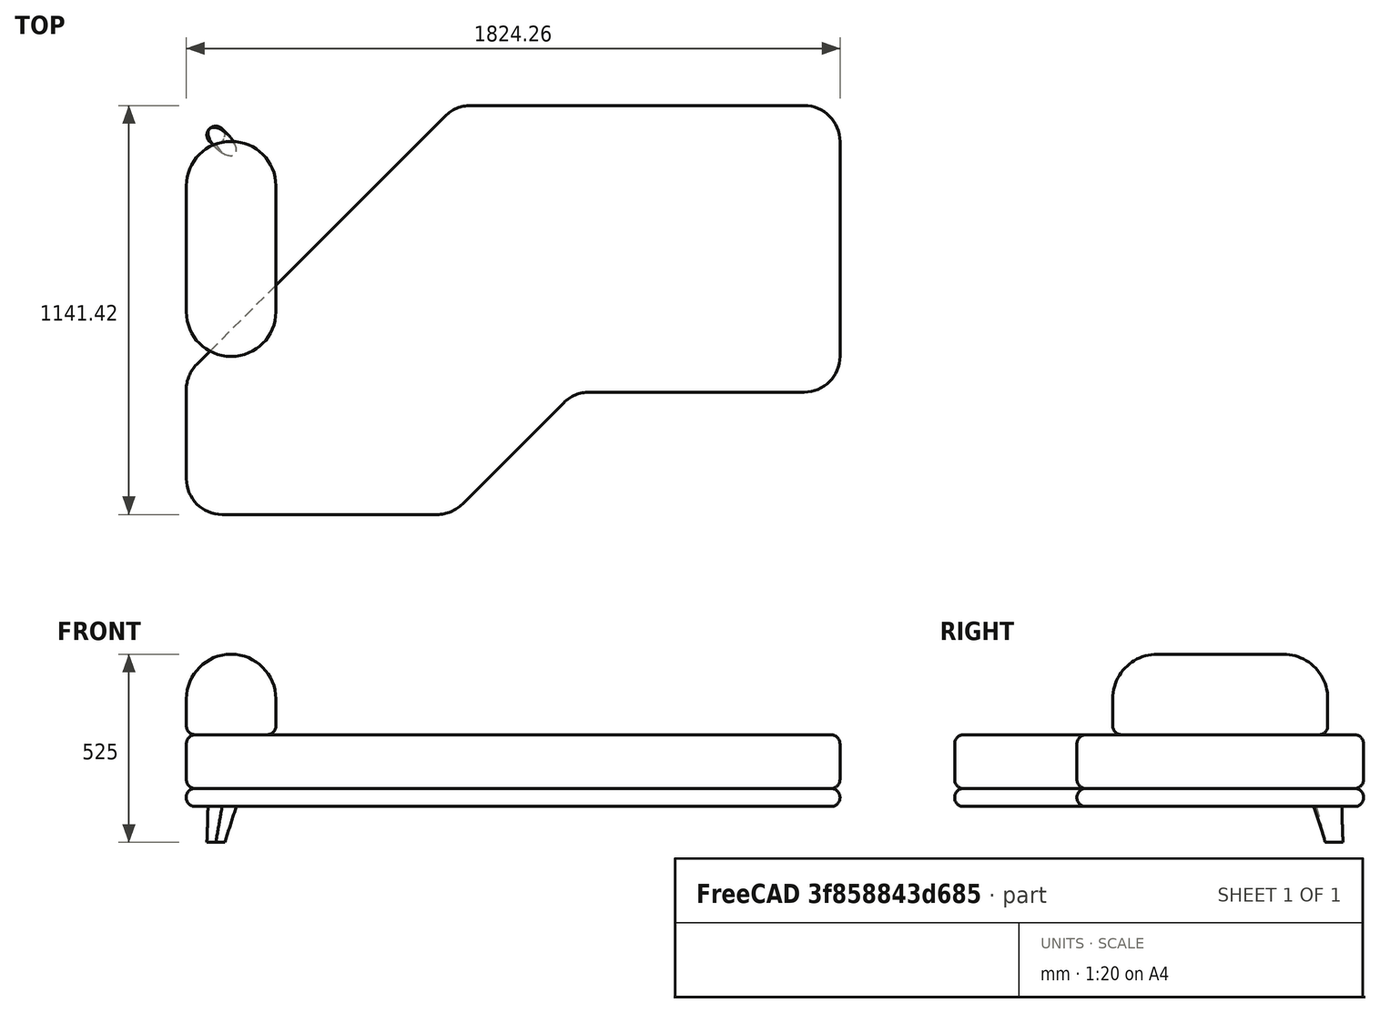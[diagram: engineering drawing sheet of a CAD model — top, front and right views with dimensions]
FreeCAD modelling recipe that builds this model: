
FCSTD DOCUMENT  (FreeCAD 1.0R39319 (Git))
Label: Drawing room Sofa corner
License: All rights reserved
objects: App::Link×10, App::FeaturePython×10, Sketcher::SketchObject×5, PartDesign::Fillet×4, PartDesign::Body×4, PartDesign::Pad×3, PartDesign::Plane×1, PartDesign::AdditiveLoft×1, Assembly::JointGroup×1, Assembly::AssemblyObject×1
note: 39 computed .brp shape members not serialized (recipe doc carries the construction recipe); baked Part::Feature solids carry a one-line shape summary decoded from their .brp

FEATURE [Sketcher::SketchObject] Sketch
  ArcFitTolerance = 1e-06
  AttachmentSupport = -> [XY_Plane]
  FullyConstrained = true
  MakeInternals = false
  MapMode = 5
  sketch-geometry (15):
    g0: ArcOfCircle CenterX=1724.26 CenterY=-100 CenterZ=0 NormalX=0 NormalY=0 NormalZ=1 AngleXU=0 Radius=100 StartAngle=1e-16 EndAngle=1.5708
    g1: LineSegment StartX=1824.26 StartY=-100 StartZ=0 EndX=1824.26 EndY=-700 EndZ=0
    g2: ArcOfCircle CenterX=1724.26 CenterY=-700 CenterZ=0 NormalX=0 NormalY=0 NormalZ=1 AngleXU=0 Radius=100 StartAngle=4.71239 EndAngle=6.28319
    g3: LineSegment StartX=1724.26 StartY=-800 StartZ=0 EndX=1124.26 EndY=-800 EndZ=0
    g4: ArcOfCircle CenterX=1124.26 CenterY=-900 CenterZ=0 NormalX=0 NormalY=0 NormalZ=1 AngleXU=0 Radius=100 StartAngle=1.5708 EndAngle=2.35619
    g5: LineSegment StartX=1053.55 StartY=-829.289 StartZ=0 EndX=770.711 EndY=-1112.13 EndZ=0
    g6: ArcOfCircle CenterX=700 CenterY=-1041.42 CenterZ=0 NormalX=0 NormalY=0 NormalZ=1 AngleXU=0 Radius=100 StartAngle=4.71239 EndAngle=5.49779
    g7: ArcOfCircle CenterX=100 CenterY=-792.893 CenterZ=0 NormalX=0 NormalY=0 NormalZ=1 AngleXU=0 Radius=100 StartAngle=2.35619 EndAngle=3.14159
    g8: LineSegment StartX=29.2893 StartY=-722.183 StartZ=0 EndX=722.183 EndY=-29.2893 EndZ=0
    g9: ArcOfCircle CenterX=792.893 CenterY=-100 CenterZ=0 NormalX=0 NormalY=0 NormalZ=1 AngleXU=0 Radius=100 StartAngle=1.5708 EndAngle=2.35619
    g10: LineSegment StartX=1724.26 StartY=0 StartZ=0 EndX=792.893 EndY=0 EndZ=0
    g11: LineSegment StartX=700 StartY=-1141.42 StartZ=0 EndX=100 EndY=-1141.42 EndZ=0
    g12: ArcOfCircle CenterX=100 CenterY=-1041.42 CenterZ=0 NormalX=0 NormalY=0 NormalZ=1 AngleXU=0 Radius=100 StartAngle=3.14159 EndAngle=4.71239
    g13: LineSegment StartX=0 StartY=-1041.42 StartZ=0 EndX=0 EndY=-792.893 EndZ=0
    g14: LineSegment [constr] StartX=0 StartY=-751.472 StartZ=0 EndX=751.472 EndY=-1.369e-13 EndZ=0
  constraints (42):
    c: Tangent(g0,g1) = 1.5708
    c: Tangent(g1,g2) = 1.5708
    c: Tangent(g2,g3) = 1.5708
    c: Tangent(g3,g4) = -1.5708
    c: Tangent(g4,g5) = -1.5708
    c: Tangent(g5,g6) = 1.5708
    c: Tangent(g7,g8) = 1.5708
    c: Tangent(g8,g9) = 1.5708
    c: Tangent(g10,g0) = -1.5708
    c: Tangent(g9,g10) = -1.5708
    c: Horizontal(g10)
    c: Vertical(g1)
    c: Horizontal(g3)
    c: Angle(g4) = 0.785398
    c: Radius(g2) = 100
    c: Radius(g0) = 100
    c: Radius(g9) = 100
    c: Parallel(g8,g5)
    c: Radius(g6) = 100
    c: Radius(g7) = 100
    c: Radius(g4) = 100
    c: Tangent(g6,g11) = 1.5708
    c: Tangent(g11,g12) = 1.5708
    c: Tangent(g12,g13) = 1.5708
    c: Vertical(g13)
    c: Horizontal(g11)
    c: Tangent(g7,g13) = 1.5708
    c: Radius(g12) = 100
    c: Distance(g1) = 600
    c: Distance(g11) = 600
    c: Distance(g3) = 600
    c: Distance(g5) = 400
    c: PointOnObject(g9,g-1)
    c: PointOnObject(g7,g-2)
    c: Distance(g4,g8) = 800
    c: PointOnObject(g14,g-2)
    c: PointOnObject(g14,g-1)
    c: PointOnObject(g14,g8)
    c: PointOnObject(g14,g8)
    c: Distance(g14,g-1) = 751.472
    c: Distance(g0,g-2) = 1824.26
    c: Distance(g11,g-1) = 1141.42
FEATURE [PartDesign::Pad] Pad
  Direction = (0,0,1)
  Length = 50
  Length2 = 10
  Profile = -> Sketch
  ReferenceAxis = -> Sketch [N_Axis]
  Refine = true
  Suppressed = false
  Type = 0
FEATURE [Sketcher::SketchObject] Sketch001
  ArcFitTolerance = 1e-06
  AttachmentSupport = -> [XY_Plane001]
  FullyConstrained = true
  MakeInternals = false
  MapMode = 5
  sketch-geometry (14):
    g0: LineSegment StartX=792.893 StartY=0 StartZ=0 EndX=1724.26 EndY=0 EndZ=0
    g1: ArcOfCircle CenterX=1724.26 CenterY=-100 CenterZ=0 NormalX=0 NormalY=0 NormalZ=1 AngleXU=0 Radius=100 StartAngle=1e-16 EndAngle=1.5708
    g2: LineSegment StartX=1824.26 StartY=-100 StartZ=0 EndX=1824.26 EndY=-700 EndZ=0
    g3: ArcOfCircle CenterX=1724.26 CenterY=-700 CenterZ=0 NormalX=0 NormalY=0 NormalZ=1 AngleXU=0 Radius=100 StartAngle=4.71239 EndAngle=6.28319
    g4: LineSegment StartX=1724.26 StartY=-800 StartZ=0 EndX=1124.26 EndY=-800 EndZ=0
    g5: ArcOfCircle CenterX=1124.26 CenterY=-900 CenterZ=0 NormalX=0 NormalY=0 NormalZ=1 AngleXU=0 Radius=100 StartAngle=1.5708 EndAngle=2.35619
    g6: LineSegment StartX=1053.55 StartY=-829.289 StartZ=0 EndX=770.711 EndY=-1112.13 EndZ=0
    g7: ArcOfCircle CenterX=700 CenterY=-1041.42 CenterZ=0 NormalX=0 NormalY=0 NormalZ=1 AngleXU=0 Radius=100 StartAngle=4.71239 EndAngle=5.49779
    g8: LineSegment StartX=700 StartY=-1141.42 StartZ=0 EndX=100 EndY=-1141.42 EndZ=0
    g9: ArcOfCircle CenterX=100 CenterY=-1041.42 CenterZ=0 NormalX=0 NormalY=0 NormalZ=1 AngleXU=0 Radius=100 StartAngle=3.14159 EndAngle=4.71239
    g10: LineSegment StartX=0 StartY=-1041.42 StartZ=0 EndX=0 EndY=-792.893 EndZ=0
    g11: ArcOfCircle CenterX=100 CenterY=-792.893 CenterZ=0 NormalX=0 NormalY=0 NormalZ=1 AngleXU=0 Radius=100 StartAngle=2.35619 EndAngle=3.14159
    g12: LineSegment StartX=29.2893 StartY=-722.183 StartZ=0 EndX=722.183 EndY=-29.2893 EndZ=0
    g13: ArcOfCircle CenterX=792.893 CenterY=-100 CenterZ=0 NormalX=0 NormalY=0 NormalZ=1 AngleXU=0 Radius=100 StartAngle=1.5708 EndAngle=2.35619
  constraints (37):
    c: PointOnObject(g0,g-1)
    c: Horizontal(g0)
    c: Tangent(g0,g1) = 1.5708
    c: Tangent(g1,g2) = 1.5708
    c: Tangent(g2,g3) = 1.5708
    c: Tangent(g3,g4) = 1.5708
    c: Tangent(g4,g5) = -1.5708
    c: Tangent(g5,g6) = -1.5708
    c: Tangent(g6,g7) = 1.5708
    c: Tangent(g7,g8) = 1.5708
    c: Tangent(g8,g9) = 1.5708
    c: Tangent(g9,g10) = 1.5708
    c: Tangent(g10,g11) = 1.5708
    c: Tangent(g11,g12) = 1.5708
    c: Tangent(g12,g13) = 1.5708
    c: Tangent(g13,g0) = 1.5708
    c: Radius(g1) = 100
    c: Radius(g3) = 100
    c: Radius(g5) = 100
    c: Radius(g7) = 100
    c: Radius(g9) = 100
    c: Radius(g11) = 100
    c: Radius(g13) = 100
    c: Horizontal(g4)
    c: Vertical(g2)
    c: Vertical(g10)
    c: Horizontal(g8)
    c: Parallel(g12,g6)
    c: Angle(g5) = 0.785398
    c: Distance(g2) = 600
    c: Distance(g4) = 600
    c: Distance(g6) = 400
    c: Distance(g5,g12) = 800
    c: Distance(g8) = 600
    c: PointOnObject(g10,g-2)
    c: Distance(g12,g12) = 979.899
    c: DistanceX(g-1,g12) = 722.183
FEATURE [PartDesign::Pad] Pad001
  Direction = (0,0,1)
  Length = 150
  Length2 = 10
  Profile = -> Sketch001
  ReferenceAxis = -> Sketch001 [N_Axis]
  Refine = true
  Suppressed = false
  Type = 0
FEATURE [PartDesign::Fillet] Fillet
  Base = -> Pad001
  BaseFeature = -> Pad001
  Radius = 25
  Refine = true
  SupportTransform = false
  Suppressed = false
  UseAllEdges = true
FEATURE [PartDesign::Body] Body001  label="Cushion"
  AllowCompound = false
  Group = -> [Sketch001,Pad001,Fillet]
  Origin = -> Origin001
  Placement = pos=(0,0,50) rot=(0,0,1;0rad)
  Tip = -> Fillet
FEATURE [PartDesign::Fillet] Fillet001
  Base = -> Pad [?Face10]
  BaseFeature = -> Pad
  Radius = 24
  Refine = true
  SupportTransform = false
  Suppressed = false
  UseAllEdges = true
FEATURE [PartDesign::Body] Body  label="Base"
  AllowCompound = false
  Group = -> [Sketch,Pad,Fillet001]
  Origin = -> Origin
  Tip = -> Fillet001
FEATURE [Sketcher::SketchObject] Sketch002
  ArcFitTolerance = 1e-06
  AttachmentSupport = -> [XZ_Plane002]
  FullyConstrained = true
  MakeInternals = false
  MapMode = 5
  Placement = pos=(0,0,0) rot=(1,0,0;1.5708rad)
  sketch-geometry (5):
    g0: LineSegment StartX=0 StartY=0 StartZ=0 EndX=250 EndY=0 EndZ=0
    g1: LineSegment StartX=250 StartY=0 StartZ=0 EndX=250 EndY=100 EndZ=0
    g2: LineSegment [constr] StartX=250 StartY=100 StartZ=0 EndX=0 EndY=100 EndZ=0
    g3: LineSegment StartX=0 StartY=100 StartZ=0 EndX=0 EndY=0 EndZ=0
    g4: ArcOfCircle CenterX=125 CenterY=100 CenterZ=0 NormalX=0 NormalY=0 NormalZ=1 AngleXU=0 Radius=125 StartAngle=0 EndAngle=3.14159
  constraints (14):
    c: Coincident(g0,g1)
    c: Coincident(g1,g2)
    c: Coincident(g2,g3)
    c: Coincident(g3,g0)
    c: Horizontal(g0)
    c: Horizontal(g2)
    c: Vertical(g1)
    c: Vertical(g3)
    c: Distance(g1,g3) = 250
    c: Distance(g0,g2) = 100
    c: Coincident(g0,g-1)
    c: Coincident(g4,g2)
    c: Coincident(g4,g1)
    c: PointOnObject(g4,g2)
FEATURE [PartDesign::Pad] Pad002
  Direction = (0,-1,2e-16)
  Length = 600
  Length2 = 10
  Placement = pos=(0,0,0) rot=(1,0,0;1.5708rad)
  Profile = -> Sketch002
  ReferenceAxis = -> Sketch002 [N_Axis]
  Refine = true
  Suppressed = false
  Type = 0
FEATURE [PartDesign::Fillet] Fillet002
  Base = -> Pad002 [Edge9,Edge10]
  BaseFeature = -> Pad002
  Placement = pos=(0,0,0) rot=(1,0,0;1.5708rad)
  Radius = 124
  Refine = true
  SupportTransform = false
  Suppressed = false
  UseAllEdges = false
FEATURE [PartDesign::Fillet] Fillet003
  Base = -> Fillet002 [Face1]
  BaseFeature = -> Fillet002
  Placement = pos=(0,0,0) rot=(1,0,0;1.5708rad)
  Radius = 25
  Refine = true
  SupportTransform = false
  Suppressed = false
  UseAllEdges = true
FEATURE [PartDesign::Body] Body002  label="Backrest"
  AllowCompound = false
  Group = -> [Sketch002,Pad002,Fillet002,Fillet003]
  Origin = -> Origin002
  Placement = pos=(0,-100,200) rot=(0,0,1;0rad)
  Tip = -> Fillet003
FEATURE [Sketcher::SketchObject] Sketch003
  ArcFitTolerance = 1e-06
  AttachmentSupport = -> [XY_Plane003]
  FullyConstrained = true
  MakeInternals = false
  MapMode = 5
  sketch-geometry (5):
    g0: Ellipse CenterX=0 CenterY=0 CenterZ=0 NormalX=0 NormalY=0 NormalZ=1 MajorRadius=50 MinorRadius=25 AngleXU=-2.35619
    g1: LineSegment [constr] StartX=-35.3553 StartY=-35.3553 StartZ=0 EndX=35.3553 EndY=35.3553 EndZ=0
    g2: LineSegment [constr] StartX=17.6777 StartY=-17.6777 StartZ=0 EndX=-17.6777 EndY=17.6777 EndZ=0
    g3: GeomPoint [constr] X=-30.6186 Y=-30.6186 Z=0
    g4: GeomPoint [constr] X=30.6186 Y=30.6186 Z=0
  constraints (5):
    c: InternalAlignment(g1-g4 -> g0) x4
    c: Distance(g0,g1) = 50
    c: Angle(g1) = 0.785398
    c: Distance(g0,g2) = 25
    c: Coincident(g0,g-1)
FEATURE [PartDesign::Plane] DatumPlane
  AttachmentOffset = pos=(0,0,-100) rot=(0,0,1;0rad)
  AttachmentSupport = -> [Sketch003]
  Length = 60
  MapMode = 2
  Placement = pos=(0,0,-100) rot=(0,0,1;0rad)
  ResizeMode = 0
  Width = 60
FEATURE [Sketcher::SketchObject] Sketch004
  ArcFitTolerance = 1e-06
  AttachmentSupport = -> [DatumPlane]
  FullyConstrained = true
  MakeInternals = false
  MapMode = 5
  Placement = pos=(0,0,-100) rot=(0,0,1;0rad)
  sketch-geometry (2):
    g0: Circle CenterX=-17.6777 CenterY=-17.6777 CenterZ=0 NormalX=0 NormalY=0 NormalZ=1 AngleXU=0 Radius=25
    g1: LineSegment [constr] StartX=-17.6777 StartY=-17.6777 StartZ=0 EndX=2.4e-15 EndY=4.5e-15 EndZ=0
  constraints (5):
    c: Diameter(g0) = 50
    c: Coincident(g1,g0)
    c: Coincident(g1,g-1)
    c: Angle(g1,g-1) = 2.35619
    c: PointOnObject(g1,g0)
FEATURE [PartDesign::AdditiveLoft] AdditiveLoft
  Closed = false
  Profile = -> Sketch003
  Refine = true
  Ruled = false
  Sections = -> [Sketch004]
  Suppressed = false
FEATURE [PartDesign::Body] Body003  label="Legs"
  AllowCompound = false
  Group = -> [Sketch003,DatumPlane,Sketch004,AdditiveLoft]
  Origin = -> Origin003
  Placement = pos=(100,-100,0) rot=(0,0,1;-1.5708rad)
  Tip = -> AdditiveLoft
FEATURE [App::Link] Base  label="Base001"
  LinkedObject = -> Body
FEATURE [App::FeaturePython] GroundedJoint  label="BaseJoint"  # Assembly grounded joint (typed FeaturePython)
  ObjectToGround = -> Base
FEATURE [App::Link] Cushion  label="Cushion001"
  LinkPlacement = pos=(0.0116274,-0.0694075,50) rot=(0,0,1;0rad)
  LinkedObject = -> Body001
  Placement = pos=(0.0116274,-0.0694075,50) rot=(0,0,1;0rad)
FEATURE [App::Link] Backrest  label="Backrest001"
  LinkPlacement = pos=(1642.13,-18.5181,200) rot=(0,0,-1;1.5708rad)
  LinkedObject = -> Body002
  Placement = pos=(1642.13,-18.5181,200) rot=(0,0,-1;1.5708rad)
FEATURE [App::Link] Legs  label="Legs001"
  LinkPlacement = pos=(1612.13,-93.5181,0) rot=(0,0,1;3.14159rad)
  LinkedObject = -> Body003
  Placement = pos=(1612.13,-93.5181,0) rot=(0,0,1;3.14159rad)
FEATURE [App::Link] Legs001  label="Legs002"
  LinkPlacement = pos=(777.126,-1013.52,0) rot=(0,0,1;1.5708rad)
  LinkedObject = -> Body003
  Placement = pos=(777.126,-1013.52,0) rot=(0,0,1;1.5708rad)
FEATURE [App::Link] Legs002  label="Legs003"
  LinkPlacement = pos=(1617.13,-693.518,0) rot=(0,0,1;1.5708rad)
  LinkedObject = -> Body003
  Placement = pos=(1617.13,-693.518,0) rot=(0,0,1;1.5708rad)
FEATURE [App::Link] Legs003  label="Legs004"
  LinkPlacement = pos=(861.126,-73.5181,0) rot=(0,0,1;4.31969rad)
  LinkedObject = -> Body003
  Placement = pos=(861.126,-73.5181,0) rot=(0,0,1;4.31969rad)
FEATURE [App::FeaturePython] Joint  label="CushionJoint"  # Assembly joint (typed FeaturePython)
  Activated = true
  AngleMax = 0
  AngleMin = 0
  Detach1 = false
  Detach2 = false
  Distance = 0
  Distance2 = 0
  EnableAngleMax = false
  EnableAngleMin = false
  EnableLengthMax = false
  EnableLengthMin = false
  JointType = 0 (Fixed)
  LengthMax = 0
  LengthMin = 0
  Placement1 = pos=(942.126,-543.518,50) rot=(0,0,1;0rad)
  Placement2 = pos=(942.114,-543.449,0) rot=(0,0,1;0rad)
  Reference1 = -> Assembly [Base.Face11,Base.Face11]
  Reference2 = -> Assembly [Cushion.Face9,Cushion.Face9]
FEATURE [App::FeaturePython] Joint001  label="BackrestJoint1"  # Assembly joint (typed FeaturePython)
  Activated = true
  AngleMax = 0
  AngleMin = 0
  Detach1 = false
  Detach2 = false
  Distance = 0
  Distance2 = 0
  EnableAngleMax = false
  EnableAngleMin = false
  EnableLengthMax = false
  EnableLengthMin = false
  JointType = 0 (Fixed)
  LengthMax = 0
  LengthMin = 0
  Offset1 = pos=(400,-400,0) rot=(0,0,1;1.5708rad)
  Placement1 = pos=(525,-700,1.448e-13) rot=(0,0,1;1.5708rad)
  Placement2 = pos=(942.114,-543.449,150) rot=(0,0,1;0rad)
  Reference1 = -> Assembly [Backrest.Face1,Backrest.Face1]
  Reference2 = -> Assembly [Cushion.Face11,Cushion.Face11]
FEATURE [App::FeaturePython] Joint002  label="LegJoint1"  # Assembly joint (typed FeaturePython)
  Activated = true
  AngleMax = 0
  AngleMin = 0
  Detach1 = false
  Detach2 = false
  Distance = 0
  Distance2 = 0
  EnableAngleMax = false
  EnableAngleMin = false
  EnableLengthMax = false
  EnableLengthMin = false
  JointType = 0 (Fixed)
  LengthMax = 0
  LengthMin = 0
  Offset1 = pos=(670,450,0) rot=(0,0,1;0rad)
  Offset2 = pos=(0,0,0) rot=(0,0,1;3.14159rad)
  Placement1 = pos=(1612.13,-93.5181,0) rot=(0,0,1;0rad)
  Placement2 = pos=(0,0,0) rot=(0,0,1;3.14159rad)
  Reference1 = -> Assembly [Base.Face9,Base.Face9]
  Reference2 = -> Assembly [Legs.Face1,Legs.Face1]
FEATURE [App::FeaturePython] Joint003  label="LegJoint2"  # Assembly joint (typed FeaturePython)
  Activated = true
  AngleMax = 0
  AngleMin = 0
  Detach1 = false
  Detach2 = false
  Distance = 0
  Distance2 = 0
  EnableAngleMax = false
  EnableAngleMin = false
  EnableLengthMax = false
  EnableLengthMin = false
  JointType = 0 (Fixed)
  LengthMax = 0
  LengthMin = 0
  Offset1 = pos=(-165,-470,0) rot=(0,0,1;1.5708rad)
  Placement1 = pos=(777.126,-1013.52,0) rot=(0,0,1;1.5708rad)
  Reference1 = -> Assembly [Base.Face9,Base.Face9]
  Reference2 = -> Assembly [Legs001.Face1,Legs001.Face1]
FEATURE [App::FeaturePython] Joint004  label="LegJoint3"  # Assembly joint (typed FeaturePython)
  Activated = true
  AngleMax = 0
  AngleMin = 0
  Detach1 = false
  Detach2 = false
  Distance = 0
  Distance2 = 0
  EnableAngleMax = false
  EnableAngleMin = false
  EnableLengthMax = false
  EnableLengthMin = false
  JointType = 0 (Fixed)
  LengthMax = 0
  LengthMin = 0
  Offset1 = pos=(675,-150,0) rot=(0,0,1;1.5708rad)
  Placement1 = pos=(1617.13,-693.518,0) rot=(0,0,1;1.5708rad)
  Reference1 = -> Assembly [Base.Face9,Base.Face9]
  Reference2 = -> Assembly [Legs002.Face1,Legs002.Face1]
FEATURE [App::FeaturePython] Joint005  label="LegJoint4"  # Assembly joint (typed FeaturePython)
  Activated = true
  AngleMax = 0
  AngleMin = 0
  Detach1 = false
  Detach2 = false
  Distance = 0
  Distance2 = 0
  EnableAngleMax = false
  EnableAngleMin = false
  EnableLengthMax = false
  EnableLengthMin = false
  JointType = 0 (Fixed)
  LengthMax = 0
  LengthMin = 0
  Offset1 = pos=(-81,470,0) rot=(0,0,-1;1.96349rad)
  Placement1 = pos=(861.126,-73.5181,0) rot=(0,0,-1;1.96349rad)
  Reference1 = -> Assembly [Base.Face9,Base.Face9]
  Reference2 = -> Assembly [Legs003.Face1,Legs003.Face1]
FEATURE [App::Link] Backrest001  label="Backrest002"
  LinkPlacement = pos=(690.869,-182.998,200) rot=(0,0,-1;0.785398rad)
  LinkedObject = -> Body002
  Placement = pos=(690.869,-182.998,200) rot=(0,0,-1;0.785398rad)
FEATURE [App::Link] Legs004  label="Legs005"
  LinkPlacement = pos=(192.126,-1018.52,0) rot=(0,0,1;0rad)
  LinkedObject = -> Body003
  Placement = pos=(192.126,-1018.52,0) rot=(0,0,1;0rad)
FEATURE [App::FeaturePython] Joint006  label="BackrestJoint2"  # Assembly joint (typed FeaturePython)
  Activated = true
  AngleMax = 0
  AngleMin = 0
  Detach1 = false
  Detach2 = false
  Distance = 0
  Distance2 = 0
  EnableAngleMax = false
  EnableAngleMin = false
  EnableLengthMax = false
  EnableLengthMin = false
  JointType = 0 (Fixed)
  LengthMax = 0
  LengthMin = 0
  Offset1 = pos=(-375,60,0) rot=(0,0,-1;0.785398rad)
  Placement1 = pos=(567.114,-483.449,150) rot=(0,0,-1;0.785398rad)
  Placement2 = pos=(125,-300,5.68e-14) rot=(0,0,1;0rad)
  Reference1 = -> Assembly [Cushion.Face11,Cushion.Face11]
  Reference2 = -> Assembly [Backrest001.Face1,Backrest001.Face1]
FEATURE [App::FeaturePython] Joint007  label="Fixed"  # Assembly joint (typed FeaturePython)
  Activated = true
  AngleMax = 0
  AngleMin = 0
  Detach1 = false
  Detach2 = false
  Distance = 0
  Distance2 = 0
  EnableAngleMax = false
  EnableAngleMin = false
  EnableLengthMax = false
  EnableLengthMin = false
  JointType = 0 (Fixed)
  LengthMax = 0
  LengthMin = 0
  Offset1 = pos=(-750,-475,0) rot=(0,0,1;0rad)
  Placement1 = pos=(192.126,-1018.52,0) rot=(0,0,1;0rad)
  Reference1 = -> Assembly [Base.Face9,Base.Face9]
  Reference2 = -> Assembly [Legs004.Face1,Legs004.Face1]
FEATURE [App::Link] Legs005  label="Legs006"
  LinkPlacement = pos=(188.179,-774.634,0) rot=(0,0,-1;1.1781rad)
  LinkedObject = -> Body003
  Placement = pos=(188.179,-774.634,0) rot=(0,0,-1;1.1781rad)
FEATURE [App::FeaturePython] Joint008  label="Fixed001"  # Assembly joint (typed FeaturePython)
  Activated = true
  AngleMax = 0
  AngleMin = 0
  Detach1 = false
  Detach2 = false
  Distance = 0
  Distance2 = 0
  EnableAngleMax = false
  EnableAngleMin = false
  EnableLengthMax = false
  EnableLengthMin = false
  JointType = 0 (Fixed)
  LengthMax = 0
  LengthMin = 0
  Offset1 = pos=(75,785,0) rot=(0,0,1;1.1781rad)
  Placement1 = pos=(75,785,0) rot=(0,0,1;1.1781rad)
  Placement2 = pos=(942.126,-543.518,0) rot=(0,0,1;0rad)
  Reference1 = -> Assembly [Legs005.Face1,Legs005.Face1]
  Reference2 = -> Assembly [Base.Face9,Base.Face9]
FEATURE [Assembly::JointGroup] Joints
  Group = -> [GroundedJoint,Joint,Joint001,Joint002,Joint003,Joint004,Joint005,Joint006,Joint007,Joint008]
FEATURE [Assembly::AssemblyObject] Assembly
  Group = -> [Joints,Base,GroundedJoint,Cushion,Backrest,Legs,Legs001,Legs002,Legs003,Joint,Joint001,Joint002,Joint003,Joint004,Joint005,Backrest001,Legs004,Joint006,Joint007,Legs005,Joint008]
  Origin = -> Origin004
  Type = Assembly
